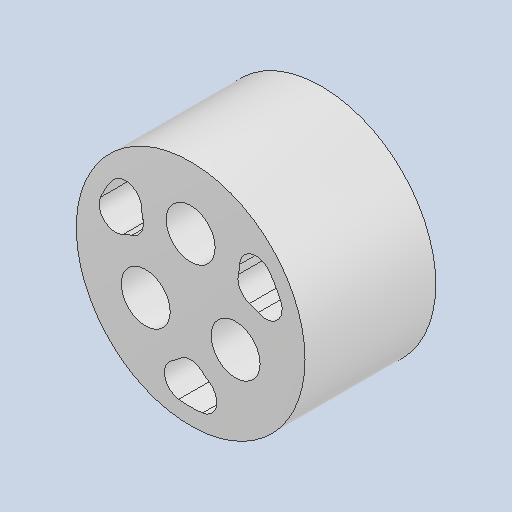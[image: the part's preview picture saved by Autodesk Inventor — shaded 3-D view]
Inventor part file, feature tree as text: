
AUTODESK INVENTOR PART (.ipt)
format: ipt  version: 2023 (Build 270158030, 158C)  size: 176,640 bytes
history: native  units: mm
features: sketch x3, other x2, extrude x2, fillet x1, projected_geometry x1
ambient origin geometry x8: Origin, YZ Plane, XZ Plane, XY Plane, X Axis, Y Axis, Z Axis, Center Point
bodies: Body1 (feature_tree)
feature tree (9):
  other  "ソリッド1"
  extrude  "押し出し1"  Depth=3.0mm
  sketch  "スケッチ2"
  extrude  "押し出し2"  Depth=3.0mm
  fillet  "フィレット1"  Radius=3.0mm
  sketch  "スケッチ1"
  projected_geometry  "投影ループ1"
  sketch  "スケッチ3"
  other  "断面エッジを投影1"
